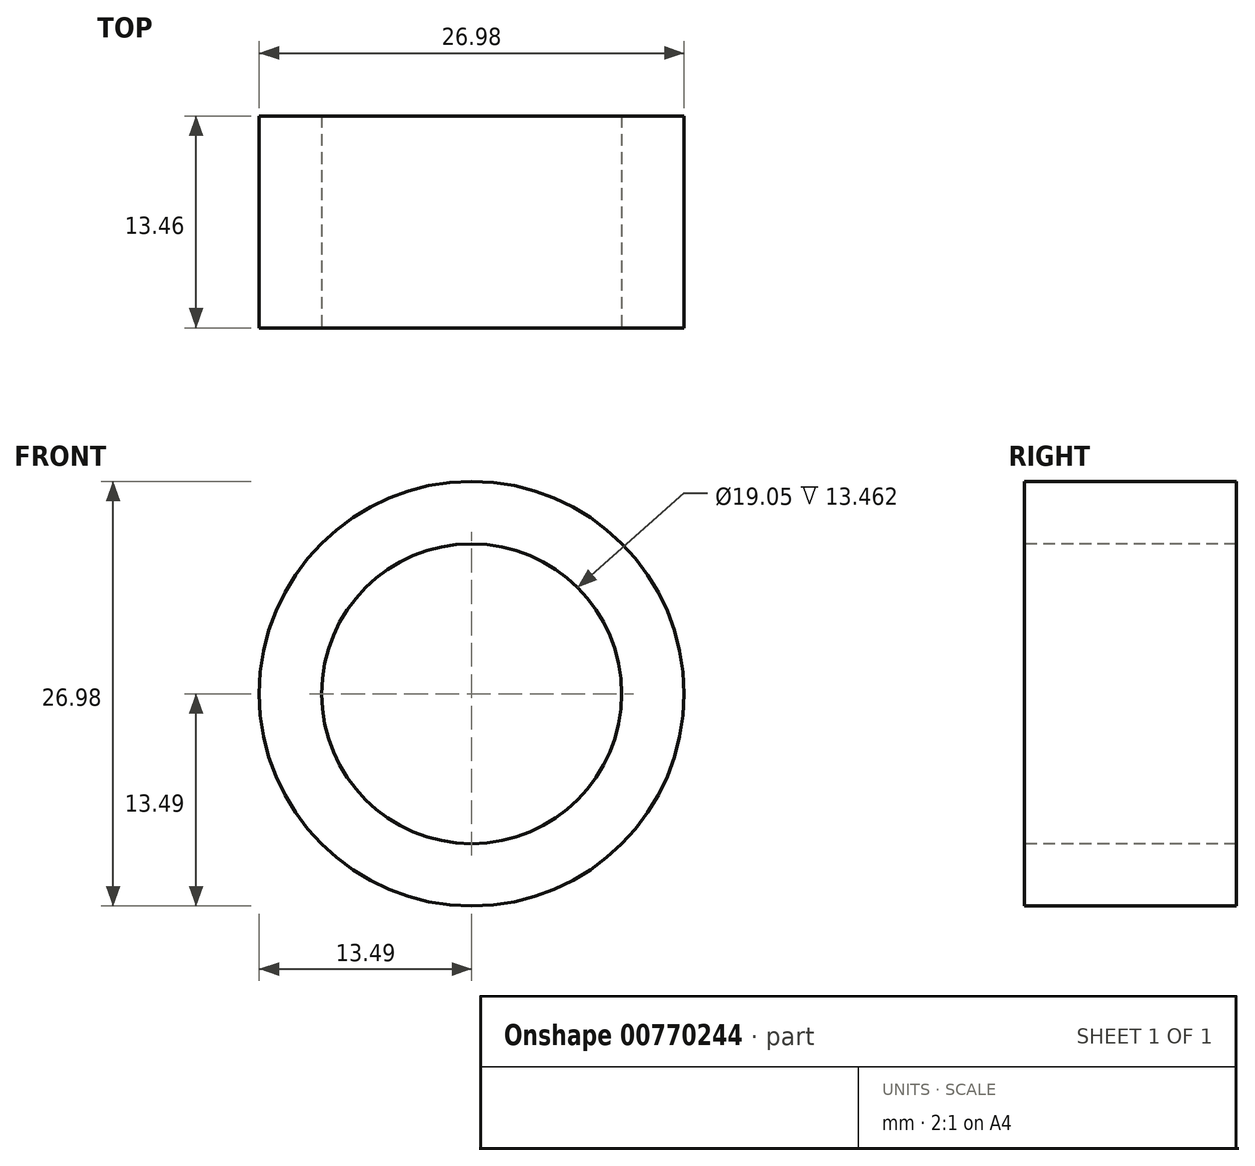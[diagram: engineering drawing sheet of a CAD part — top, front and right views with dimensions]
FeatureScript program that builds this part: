
annotation { "Feature Type Name" : "Feature", "Feature Type Description" : "" }
export const myFeature = defineFeature(function(context is Context, id is Id, definition is map)
    precondition{}
    {
        {
            var Q0;
            Q0=qCreatedBy(makeId("Front.planeOp"),FACE);
            var sketch = newSketch(context, id + "F0", { "sketchPlane" : qUnion([Q0])});
            skCircle(sketch, "E0", {"center": v(0, 0) * mm, "radius": 13.49 * mm});
            skSolve(sketch);
        }
        {
            var Q0;
            Q0=makeQuery(id+"F0.imprint","IMPRINT",FACE,{"disambiguationData":[TD([[makeQuery(id+"F0.imprint","IMPRINT",EDGE,{"derivedFrom":sQuery(id+"F0.wireOp",EDGE,"E0")}),1.0]])]});
            var Q1;
            Q1=sQuery(id+"F0.wireOp",EDGE,"E0");
            extrude(context, id + "F1", {"entities" : qUnion([Q0]), "surfaceEntities" : qUnion([Q1]), "endBound" : BoundingType.SYMMETRIC, "depth" : 13.46 * mm});
        }
        {
            var Q0;
            Q0=makeQuery(id+"F1.opExtrude","CAP_FACE",FACE,{"disambiguationData":[OSD([sQuery(id+"F0.wireOp",EDGE,"E0")])],"isStart":false});
            var sketch = newSketch(context, id + "F2", { "sketchPlane" : qUnion([Q0])});
            skCircle(sketch, "E1", {"center": v(0, 0) * mm, "radius": 9.52 * mm});
            skSolve(sketch);
        }
        {
            var Q0;
            Q0=makeQuery(id+"F2.imprint","IMPRINT",FACE,{"disambiguationData":[TD([[makeQuery(id+"F2.imprint","IMPRINT",EDGE,{"derivedFrom":sQuery(id+"F2.wireOp",EDGE,"E1")}),1.0]])]});
            extrude(context, id + "F3", {"entities" : qUnion([Q0]), "operationType" : NewBodyOperationType.REMOVE, "oppositeDirection" : true, "depth" : 13.46 * mm});
        }
    });
